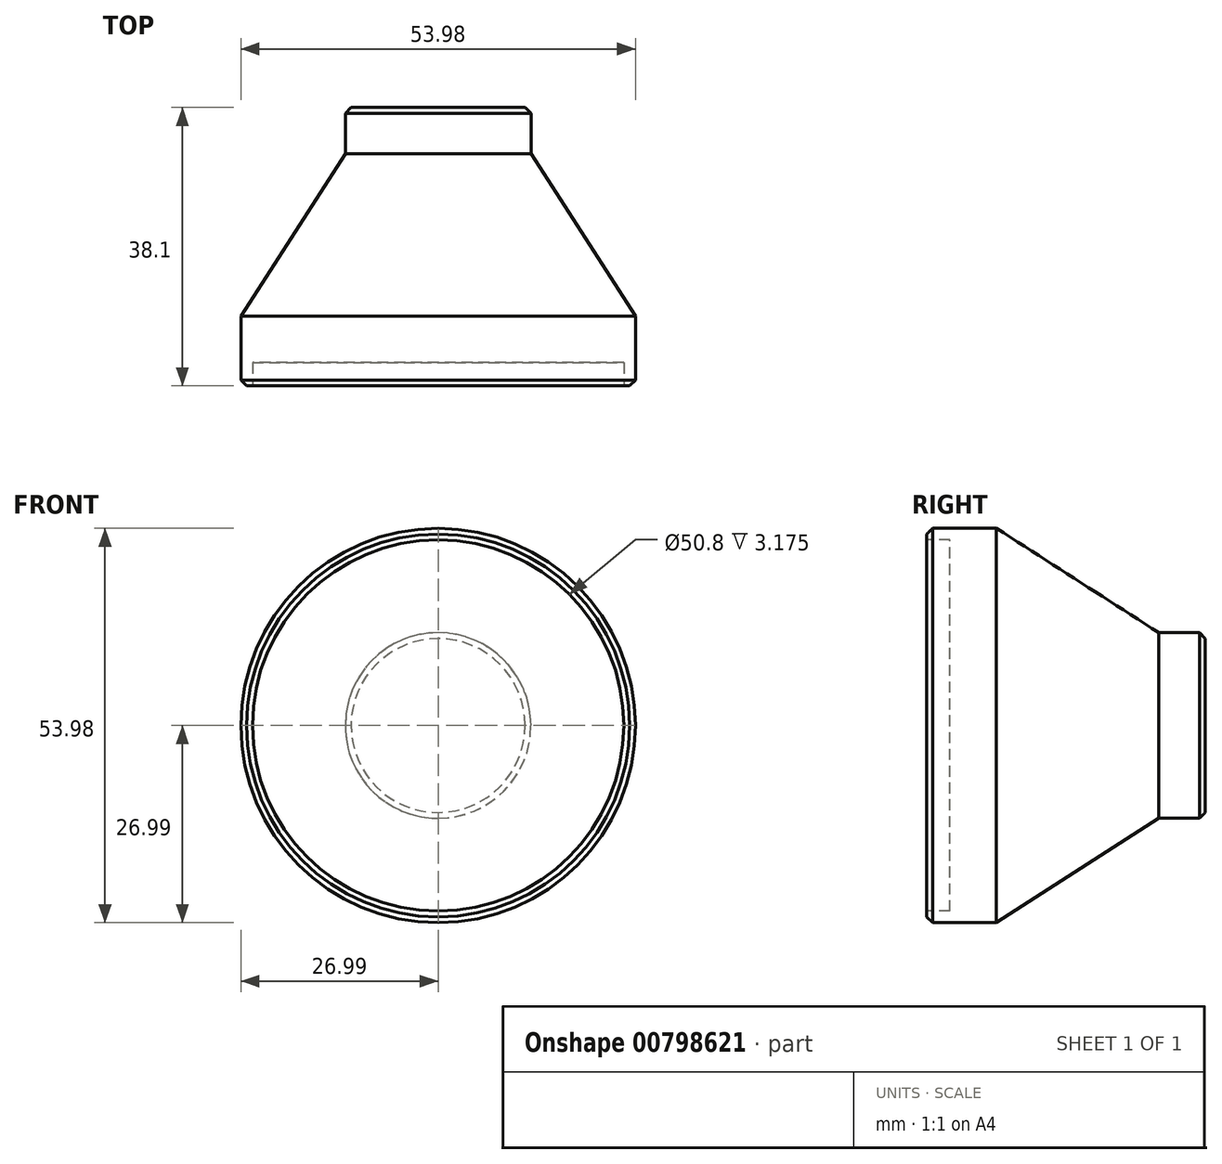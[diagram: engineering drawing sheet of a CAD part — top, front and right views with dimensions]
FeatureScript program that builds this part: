
annotation { "Feature Type Name" : "Feature", "Feature Type Description" : "" }
export const myFeature = defineFeature(function(context is Context, id is Id, definition is map)
    precondition{}
    {
        {
            var Q0;
            Q0=qCreatedBy(makeId("Right.planeOp"),FACE);
            var sketch = newSketch(context, id + "F0", { "sketchPlane" : qUnion([Q0])});
            skLineSegment(sketch, "E0", {"start": v(0, 0) * mm, "end": v(0, 26.99) * mm});
            skLineSegment(sketch, "E1", {"start": v(0, 26.99) * mm, "end": v(9.53, 26.99) * mm});
            skLineSegment(sketch, "E2", {"start": v(9.52, 26.99) * mm, "end": v(31.75, 12.7) * mm});
            skLineSegment(sketch, "E3", {"start": v(31.75, 12.7) * mm, "end": v(38.1, 12.7) * mm});
            skLineSegment(sketch, "E4", {"start": v(38.1, 12.7) * mm, "end": v(38.1, 0) * mm});
            skLineSegment(sketch, "E5", {"start": v(38.1, 0) * mm, "end": v(0, 0) * mm});
            skSolve(sketch);
        }
        {
            var Q0;
            Q0 = qSketchRegion(id + "F0", true);
            var Q1;
            Q1=sQuery(id+"F0.wireOp",EDGE,"E5");
            revolve(context, id + "F1", {"surfaceOperationType" : NewSurfaceOperationType.NEW, "entities" : qUnion([Q0]), "axis" : qUnion([Q1]), "revolveType" : RevolveType.FULL});
        }
        {
            var Q0;
            Q0=makeQuery(id+"F1.opRevolve","SWEPT_FACE",FACE,{"disambiguationData":[OSD([sQuery(id+"F0.wireOp",EDGE,"E0")])]});
            var sketch = newSketch(context, id + "F2", { "sketchPlane" : qUnion([Q0])});
            skCircle(sketch, "E6", {"center": v(0, 0) * mm, "radius": 25.4 * mm});
            skSolve(sketch);
        }
        {
            var Q0;
            Q0 = qSketchRegion(id + "F2", true);
            extrude(context, id + "F3", {"entities" : qUnion([Q0]), "operationType" : NewBodyOperationType.REMOVE, "oppositeDirection" : true, "depth" : 3.17 * mm, "offsetDistance" : 25.4 * mm});
        }
        {
            var Q0;
            Q0=makeQuery(id+"F1.opRevolve","SWEPT_EDGE",EDGE,{"disambiguationData":[OSD([sQuery(id+"F0.wireOp",EDGE,"E0"),sQuery(id+"F0.wireOp",EDGE,"E1")])]});
            var Q1;
            Q1=makeQuery(id+"F1.opRevolve","SWEPT_EDGE",EDGE,{"disambiguationData":[OSD([sQuery(id+"F0.wireOp",EDGE,"E3"),sQuery(id+"F0.wireOp",EDGE,"E4")])]});
            chamfer(context, id + "F4", {"entities" : qUnion([Q0, Q1]), "width" : 0.8 * mm, "tangentPropagation" : true});
        }
    });
